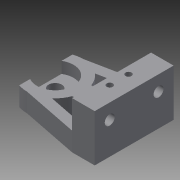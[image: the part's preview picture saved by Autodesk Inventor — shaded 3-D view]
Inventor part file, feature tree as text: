
AUTODESK INVENTOR PART (.ipt)
format: ipt  version: 2015 (Build 190159000, 159)  size: 164,352 bytes
history: native  units: in
note: dims shown in document units (in); Inventor stores cm internally (conversion verified against a paired STEP export)
features: extrude x5, sketch x3
ambient origin geometry x8: Origin, YZ Plane, XZ Plane, XY Plane, X Axis, Y Axis, Z Axis, Center Point
bodies: Solid1 (feature_tree)
feature tree (8):
  extrude  "Extrusion1"  Depth=0.4724in
  sketch  "Sketch2"  dims[d2=0.1969in d3=0.1969in]
  extrude  "Extrusion2"  Depth=0.1969in
  extrude  "Extrusion4"  Depth=0.2362in
  extrude  "Extrusion5"  Depth=0.2362in
  extrude  "Extrusion6"  Depth=0.2362in
  sketch  "Sketch1"  dims[d0=1.6535in d1=0.4724in]
  sketch  "Sketch3"  dims[d4=0.1181in d5=0.1181in d6=0.1181in d7=0.1181in d8=0.1575in d9=0.126in d10=0.126in d11=0.5906in d12=0.0in d13=1.1811in d14=0.2756in d16=1.1811in d17=0.1969in d18=0.3937in d19=0.0in d22=0.5118in d23=0.2756in d24=0.5118in d25=0.2756in d26=0.2087in d27=0.2087in d28=0.5906in d29=0.0in d30=0.2165in d31=0.2165in d32=0.3937in d33=0.1969in d34=0.5906in d35=0.0in d36=0.7677in d37=0.2362in d38=0.0in]
